# Revit family: Вентиляційна установка 0010016045 recoVAIR VAR360 0010016046 recoVAIR VAR260
name_source: partatom
category: Оборудование
units: mm (PartAtom-declared; Revit-internal decimal feet)

## family parameters
Всегда вертикально = Да
Заголовок OmniClass = Heat Exchangers for Ventilation Air
На основе рабочей плоскости = Нет
Номер OmniClass = 23.75.10.34.21
Общий = Нет
При загрузке вырезать с полостями = Нет
Размер круглого соединителя = Использовать диаметр
Сохранять ориентацию аннотаций = Нет
Тип детали = Нормальный
Точка принадлежности помещению = Нет

## types (2) — shared parameters
Article Description = Припливно-витяжна вентиляційна установка
Base Family Version = 22.08
Black = Color RGB 040-040-040
Connection Pipes = Color RGB 116-051-029
Content Supplier URL = www.MEPcontent.com
Custom = Нет
Depth = 631 мм
Diameter = 180 мм
Drain Diameter = 32 мм
EMCS Version = 4.0
ETIM Article Class = EC011285
Family Version = 12.05
GLN = 4024074000007
Grey = Color RGB 121-121-121
Heating Power = 500 Вт
Height = 885 мм
IFCExportAs = IfcAirToAirHeatRecovery
IFCExportType = NOTDEFINED
MEPcontent Class = AIR_HEATER_HEAT_RECOVERY
Manufacturer URL = https://www.vaillant.ua
Product Line = recoVAIR
Revit Version = 2020
URL = https://mep.trimble.com
Voltage = 230 В
White = Color RGB 244-244-244
Width = 595 мм
Изготовитель = Vaillant
Описание = Припливно-витяжна вентиляційна установка
zero-valued in all types: Отметка по умолчанию

## per-type parameters (varying)
| type | Heating Device Type | Manufacturer Art. No. | Power |
| recoVAIR VAR 260-4 | VE_Air Heater_MEPcontent_Vaillant_Heating Device 1000 W-1500 W : 1000 W | 0010016046 | 170 В·А |
| recoVAIR VAR 360-4 | VE_Air Heater_MEPcontent_Vaillant_Heating Device 1000 W-1500 W : 1500 W | 0010016045 | 342 В·А |

note: column(s) folded — value = type name in every type: Article Type, Группа модели

## geometry (parser evidence)
native form markers: Sweep x8
no freeform markers — native parametric forms only
